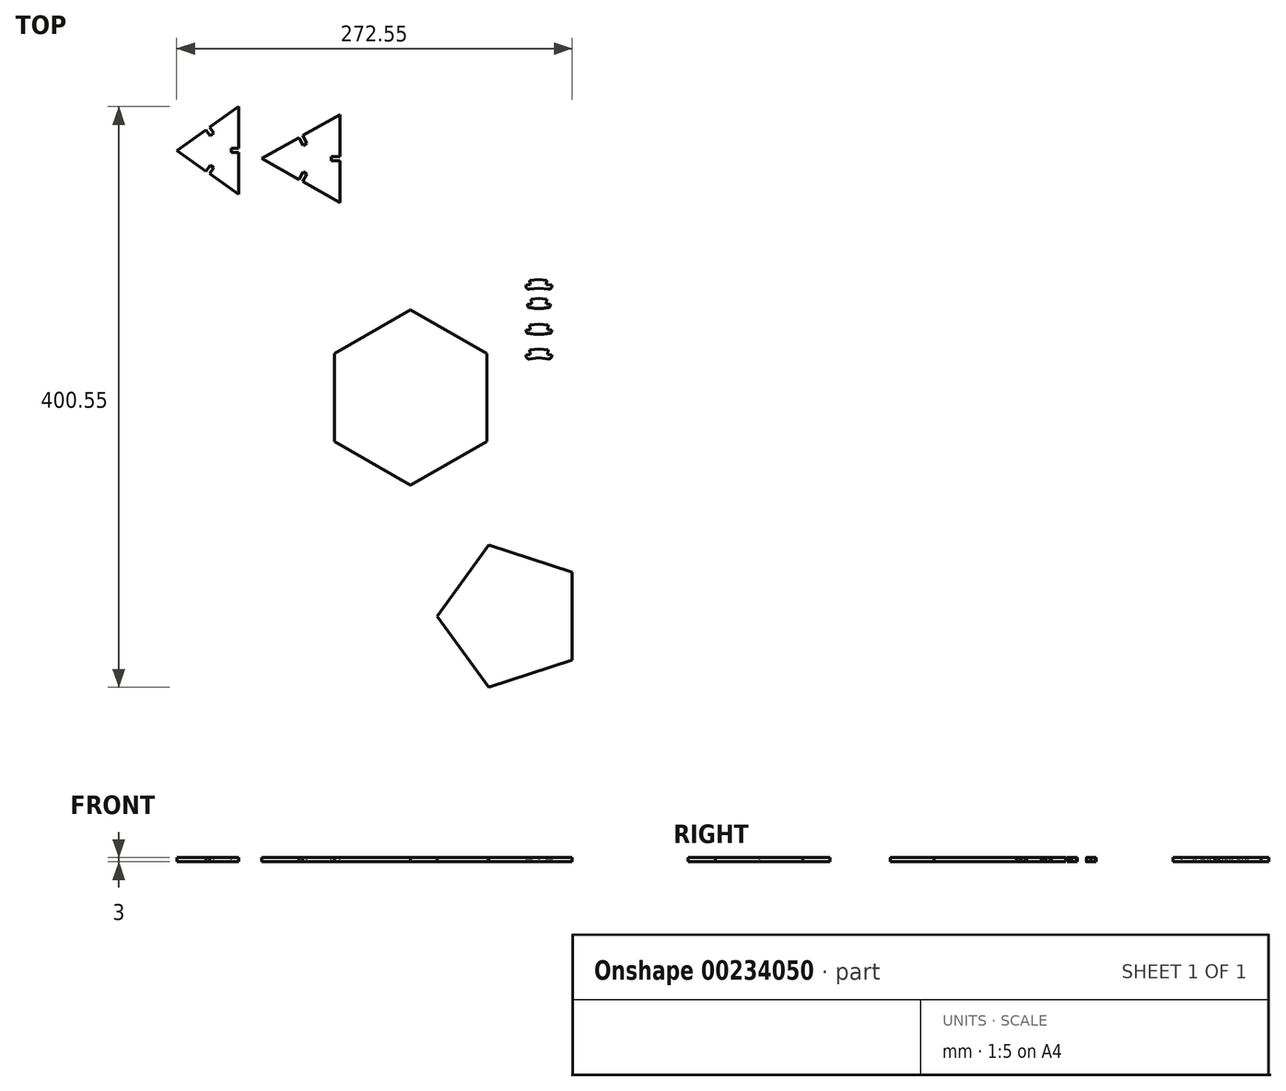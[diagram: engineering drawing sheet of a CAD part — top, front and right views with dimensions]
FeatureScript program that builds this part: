
annotation { "Feature Type Name" : "Feature", "Feature Type Description" : "" }
export const myFeature = defineFeature(function(context is Context, id is Id, definition is map)
    precondition{}
    {
        {
            var Q0;
            Q0=qCreatedBy(makeId("Top.planeOp"),FACE);
            var sketch = newSketch(context, id + "F0", { "sketchPlane" : qUnion([Q0])});
            skLineSegment(sketch, "E0", {"start": v(0, 0) * mm, "end": v(49.36, 17.26) * mm});
            skLineSegment(sketch, "E1", {"start": v(0, 0) * mm, "end": v(32.59, -40.9) * mm});
            skLineSegment(sketch, "E2", {"start": v(0, 0) * mm, "end": v(0, 52.3) * mm});
            skLineSegment(sketch, "E3", {"start": v(0, 52.3) * mm, "end": v(49.36, 17.26) * mm});
            skLineSegment(sketch, "E4", {"start": v(49.36, 17.26) * mm, "end": v(32.59, -40.9) * mm});
            skLineSegment(sketch, "E5", {"start": v(0, 0) * mm, "end": v(-27.84, -44.26) * mm});
            skLineSegment(sketch, "E6", {"start": v(-27.84, -44.26) * mm, "end": v(32.59, -40.9) * mm});
            skLineSegment(sketch, "E7", {"start": v(32.59, -40.9) * mm, "end": v(-27.84, -44.26) * mm});
            skLineSegment(sketch, "E8", {"start": v(-27.84, -44.26) * mm, "end": v(-50.97, 11.67) * mm});
            skLineSegment(sketch, "E9", {"start": v(-50.97, 11.67) * mm, "end": v(0, 0) * mm});
            skLineSegment(sketch, "E10", {"start": v(-50.97, 11.67) * mm, "end": v(-5.8, 51.97) * mm});
            skLineSegment(sketch, "E11", {"start": v(-5.8, 51.97) * mm, "end": v(0, 0) * mm});
            skLineSegment(sketch, "E12", {"start": v(-5.8, 51.97) * mm, "end": v(0, 52.3) * mm});
            skSolve(sketch);
        }
        {
            var Q0;
            Q0=qCreatedBy(makeId("Top.planeOp"),FACE);
            var sketch = newSketch(context, id + "F1", { "sketchPlane" : qUnion([Q0])});
            skLineSegment(sketch, "E13.0", {"start": v(0, 52.3) * mm, "end": v(49.36, 17.26) * mm});
            skLineSegment(sketch, "E14", {"start": v(0, 52.3) * mm, "end": v(55.9, 78.77) * mm});
            skLineSegment(sketch, "E15", {"start": v(55.9, 78.77) * mm, "end": v(49.36, 17.26) * mm});
            skLineSegment(sketch, "E16", {"start": v(55.9, 78.77) * mm, "end": v(104.98, 41.12) * mm});
            skLineSegment(sketch, "E17", {"start": v(104.98, 41.12) * mm, "end": v(49.36, 17.26) * mm});
            skLineSegment(sketch, "E18", {"start": v(55.9, 78.77) * mm, "end": v(4.16, 112.67) * mm});
            skLineSegment(sketch, "E19", {"start": v(4.16, 112.67) * mm, "end": v(0, 52.3) * mm});
            skLineSegment(sketch, "E20", {"start": v(55.9, 78.77) * mm, "end": v(57.85, 140.6) * mm});
            skLineSegment(sketch, "E21", {"start": v(57.85, 140.6) * mm, "end": v(4.16, 112.67) * mm});
            skLineSegment(sketch, "E22", {"start": v(55.9, 78.77) * mm, "end": v(113.62, 101.02) * mm});
            skLineSegment(sketch, "E23", {"start": v(113.62, 101.02) * mm, "end": v(104.98, 41.12) * mm});
            skLineSegment(sketch, "E24", {"start": v(55.9, 78.77) * mm, "end": v(67, 139.63) * mm});
            skLineSegment(sketch, "E25", {"start": v(67, 139.63) * mm, "end": v(113.62, 101.02) * mm});
            skLineSegment(sketch, "E26.0.2", {"start": v(49.36, 17.26) * mm, "end": v(0, 52.3) * mm, "construction": true});
            skLineSegment(sketch, "E27", {"start": v(67, 139.63) * mm, "end": v(124.73, 161.88) * mm});
            skLineSegment(sketch, "E28", {"start": v(124.73, 161.88) * mm, "end": v(113.62, 101.02) * mm});
            skLineSegment(sketch, "E29", {"start": v(67, 139.63) * mm, "end": v(75.65, 199.53) * mm});
            skLineSegment(sketch, "E30", {"start": v(75.65, 199.53) * mm, "end": v(124.73, 161.88) * mm});
            skLineSegment(sketch, "E31", {"start": v(113.62, 101.02) * mm, "end": v(170.87, 120.68) * mm});
            skLineSegment(sketch, "E32", {"start": v(170.87, 120.68) * mm, "end": v(124.73, 161.88) * mm});
            skLineSegment(sketch, "E33", {"start": v(4.16, 112.67) * mm, "end": v(11.33, 164.47) * mm});
            skLineSegment(sketch, "E34", {"start": v(11.33, 164.47) * mm, "end": v(57.85, 140.6) * mm});
            skLineSegment(sketch, "E35", {"start": v(67, 139.63) * mm, "end": v(29.12, 175.67) * mm});
            skLineSegment(sketch, "E36", {"start": v(29.12, 175.67) * mm, "end": v(75.65, 199.53) * mm});
            skLineSegment(sketch, "E37", {"start": v(104.98, 41.12) * mm, "end": v(151.5, 64.98) * mm});
            skLineSegment(sketch, "E38", {"start": v(151.5, 64.98) * mm, "end": v(113.62, 101.02) * mm});
            skLineSegment(sketch, "E39", {"start": v(113.62, 101.02) * mm, "end": v(156.1, 70.52) * mm});
            skLineSegment(sketch, "E40", {"start": v(156.1, 70.52) * mm, "end": v(170.87, 120.68) * mm});
            skLineSegment(sketch, "E41", {"start": v(156.1, 70.52) * mm, "end": v(206.92, 82.8) * mm});
            skLineSegment(sketch, "E42", {"start": v(206.92, 82.8) * mm, "end": v(170.87, 120.68) * mm});
            skLineSegment(sketch, "E43", {"start": v(0, 52.3) * mm, "end": v(0, 0) * mm});
            skLineSegment(sketch, "E44", {"start": v(0, 0) * mm, "end": v(49.36, 17.26) * mm});
            skLineSegment(sketch, "E45", {"start": v(124.73, 161.88) * mm, "end": v(131.27, 223.4) * mm});
            skLineSegment(sketch, "E46", {"start": v(124.73, 161.88) * mm, "end": v(180.63, 188.36) * mm});
            skLineSegment(sketch, "E47", {"start": v(75.65, 199.53) * mm, "end": v(131.27, 223.4) * mm});
            skLineSegment(sketch, "E48", {"start": v(180.63, 188.36) * mm, "end": v(176.47, 127.98) * mm});
            skLineSegment(sketch, "E49", {"start": v(176.47, 127.98) * mm, "end": v(124.73, 161.88) * mm});
            skLineSegment(sketch, "E50", {"start": v(131.27, 223.4) * mm, "end": v(180.63, 188.36) * mm});
            skLineSegment(sketch, "E51", {"start": v(75.65, 199.53) * mm, "end": v(82.2, 261.05) * mm});
            skLineSegment(sketch, "E52", {"start": v(82.2, 261.05) * mm, "end": v(131.27, 223.4) * mm});
            skLineSegment(sketch, "E53", {"start": v(176.47, 127.98) * mm, "end": v(232.38, 154.47) * mm});
            skLineSegment(sketch, "E54", {"start": v(232.38, 154.47) * mm, "end": v(180.63, 188.36) * mm});
            skLineSegment(sketch, "E55", {"start": v(176.47, 127.98) * mm, "end": v(225.83, 92.95) * mm});
            skLineSegment(sketch, "E56", {"start": v(225.83, 92.95) * mm, "end": v(232.38, 154.47) * mm});
            skLineSegment(sketch, "E57.1.0", {"start": v(0, 0) * mm, "end": v(21.73, -27.26) * mm});
            skLineSegment(sketch, "E57.1.1", {"start": v(48.98, -57.01) * mm, "end": v(21.73, -27.26) * mm});
            skLineSegment(sketch, "E57.1.2", {"start": v(61.88, -17.84) * mm, "end": v(21.73, -27.26) * mm});
            skLineSegment(sketch, "E57.1.3", {"start": v(21.73, -27.26) * mm, "end": v(32.9, 11.5) * mm, "construction": true});
            skLineSegment(sketch, "E57.1.4", {"start": v(48.98, -57.01) * mm, "end": v(74.24, -81.04) * mm});
            skLineSegment(sketch, "E57.1.5", {"start": v(88.58, -49.27) * mm, "end": v(48.98, -57.01) * mm});
            skLineSegment(sketch, "E57.1.6", {"start": v(32.9, 11.5) * mm, "end": v(61.88, -17.84) * mm});
            skLineSegment(sketch, "E57.1.7", {"start": v(71.82, 22.18) * mm, "end": v(32.9, 11.5) * mm});
            skLineSegment(sketch, "E57.1.8", {"start": v(61.88, -17.84) * mm, "end": v(48.98, -57.01) * mm});
            skLineSegment(sketch, "E57.1.9", {"start": v(78.73, -82.7) * mm, "end": v(113.55, -80.97) * mm});
            skLineSegment(sketch, "E57.1.10", {"start": v(61.88, -17.84) * mm, "end": v(102.62, -11.44) * mm});
            skLineSegment(sketch, "E57.1.11", {"start": v(119.38, -82.89) * mm, "end": v(108.2, -121.66) * mm});
            skLineSegment(sketch, "E57.1.12", {"start": v(61.88, -17.84) * mm, "end": v(71.82, 22.18) * mm});
            skLineSegment(sketch, "E57.1.13", {"start": v(61.88, -17.84) * mm, "end": v(88.58, -49.27) * mm});
            skLineSegment(sketch, "E57.1.14", {"start": v(88.58, -49.27) * mm, "end": v(113.55, -80.97) * mm});
            skLineSegment(sketch, "E57.1.15", {"start": v(108.2, -121.66) * mm, "end": v(148.35, -112.24) * mm});
            skLineSegment(sketch, "E57.1.16", {"start": v(102.62, -11.44) * mm, "end": v(88.58, -49.27) * mm});
            skLineSegment(sketch, "E57.1.17", {"start": v(129.32, -42.86) * mm, "end": v(88.58, -49.27) * mm});
            skLineSegment(sketch, "E57.1.18", {"start": v(97.65, -111.99) * mm, "end": v(113.55, -80.97) * mm});
            skLineSegment(sketch, "E57.1.19", {"start": v(61.88, -17.84) * mm, "end": v(101.21, -5.46) * mm});
            skLineSegment(sketch, "E57.1.20", {"start": v(71.82, 22.18) * mm, "end": v(106, 29.07) * mm});
            skLineSegment(sketch, "E57.1.21", {"start": v(101.21, -5.46) * mm, "end": v(71.82, 22.18) * mm});
            skLineSegment(sketch, "E57.1.22", {"start": v(119.38, -82.89) * mm, "end": v(148.35, -112.24) * mm});
            skLineSegment(sketch, "E57.1.23", {"start": v(158.3, -72.21) * mm, "end": v(119.38, -82.89) * mm});
            skLineSegment(sketch, "E57.1.24", {"start": v(102.62, -11.44) * mm, "end": v(129.32, -42.86) * mm});
            skLineSegment(sketch, "E57.1.25", {"start": v(106, 29.07) * mm, "end": v(101.21, -5.46) * mm});
            skLineSegment(sketch, "E57.1.26", {"start": v(102.62, -11.44) * mm, "end": v(142.21, -3.69) * mm});
            skLineSegment(sketch, "E57.1.27", {"start": v(148.35, -112.24) * mm, "end": v(158.3, -72.21) * mm});
            skLineSegment(sketch, "E57.1.28", {"start": v(142.21, -3.69) * mm, "end": v(129.32, -42.86) * mm});
            skLineSegment(sketch, "E57.1.29", {"start": v(129.32, -42.86) * mm, "end": v(158.3, -72.21) * mm});
            skLineSegment(sketch, "E57.1.30", {"start": v(129.32, -42.86) * mm, "end": v(169.47, -33.44) * mm});
            skLineSegment(sketch, "E57.1.31", {"start": v(116.96, 20.34) * mm, "end": v(142.21, -3.69) * mm});
            skLineSegment(sketch, "E57.1.32", {"start": v(142.21, -3.69) * mm, "end": v(169.47, -33.44) * mm});
            skLineSegment(sketch, "E57.1.33", {"start": v(142.21, -3.69) * mm, "end": v(182.36, 5.73) * mm});
            skLineSegment(sketch, "E57.1.34", {"start": v(169.47, -33.44) * mm, "end": v(158.3, -72.21) * mm});
            skLineSegment(sketch, "E57.1.35", {"start": v(182.36, 5.73) * mm, "end": v(169.47, -33.44) * mm});
            skLineSegment(sketch, "E57.1.36", {"start": v(32.9, 11.5) * mm, "end": v(21.73, -27.26) * mm});
            skLineSegment(sketch, "E57.1.37", {"start": v(74.24, -81.04) * mm, "end": v(88.58, -49.27) * mm});
            skLineSegment(sketch, "E57.1.38", {"start": v(78.73, -82.7) * mm, "end": v(97.65, -111.99) * mm});
            skLineSegment(sketch, "E57.1.39", {"start": v(88.58, -49.27) * mm, "end": v(78.73, -82.7) * mm});
            skLineSegment(sketch, "E57.1.40", {"start": v(113.55, -80.97) * mm, "end": v(129.32, -42.86) * mm});
            skLineSegment(sketch, "E57.1.41", {"start": v(119.38, -82.89) * mm, "end": v(129.32, -42.86) * mm});
            skLineSegment(sketch, "E57.1.42", {"start": v(102.62, -11.44) * mm, "end": v(116.96, 20.34) * mm});
            skLineSegment(sketch, "E57.2.0", {"start": v(0, 0) * mm, "end": v(-18.56, -29.5) * mm});
            skLineSegment(sketch, "E57.2.1", {"start": v(-37.65, -65.06) * mm, "end": v(-18.56, -29.5) * mm});
            skLineSegment(sketch, "E57.2.2", {"start": v(3.59, -64.3) * mm, "end": v(-18.56, -29.5) * mm});
            skLineSegment(sketch, "E57.2.3", {"start": v(-18.56, -29.5) * mm, "end": v(21.73, -27.26) * mm, "construction": true});
            skLineSegment(sketch, "E57.2.4", {"start": v(-37.65, -65.06) * mm, "end": v(-51.99, -96.83) * mm});
            skLineSegment(sketch, "E57.2.5", {"start": v(-17.26, -99.88) * mm, "end": v(-37.65, -65.06) * mm});
            skLineSegment(sketch, "E57.2.6", {"start": v(21.73, -27.26) * mm, "end": v(3.59, -64.3) * mm});
            skLineSegment(sketch, "E57.2.7", {"start": v(44.65, -60.47) * mm, "end": v(21.73, -27.26) * mm});
            skLineSegment(sketch, "E57.2.8", {"start": v(3.59, -64.3) * mm, "end": v(-37.65, -65.06) * mm});
            skLineSegment(sketch, "E57.2.9", {"start": v(-52.08, -101.62) * mm, "end": v(-38.94, -133.91) * mm});
            skLineSegment(sketch, "E57.2.10", {"start": v(3.59, -64.3) * mm, "end": v(23.08, -100.64) * mm});
            skLineSegment(sketch, "E57.2.11", {"start": v(-38.83, -140.05) * mm, "end": v(-79.11, -142.3) * mm});
            skLineSegment(sketch, "E57.2.12", {"start": v(3.59, -64.3) * mm, "end": v(44.65, -60.47) * mm});
            skLineSegment(sketch, "E57.2.13", {"start": v(3.59, -64.3) * mm, "end": v(-17.26, -99.88) * mm});
            skLineSegment(sketch, "E57.2.14", {"start": v(-17.26, -99.88) * mm, "end": v(-38.94, -133.91) * mm});
            skLineSegment(sketch, "E57.2.15", {"start": v(-79.11, -142.3) * mm, "end": v(-56.97, -177.08) * mm});
            skLineSegment(sketch, "E57.2.16", {"start": v(23.08, -100.64) * mm, "end": v(-17.26, -99.88) * mm});
            skLineSegment(sketch, "E57.2.17", {"start": v(2.23, -136.22) * mm, "end": v(-17.26, -99.88) * mm});
            skLineSegment(sketch, "E57.2.18", {"start": v(-73.47, -129.14) * mm, "end": v(-38.94, -133.91) * mm});
            skLineSegment(sketch, "E57.2.19", {"start": v(3.59, -64.3) * mm, "end": v(28.26, -97.34) * mm});
            skLineSegment(sketch, "E57.2.20", {"start": v(44.65, -60.47) * mm, "end": v(62.43, -90.45) * mm});
            skLineSegment(sketch, "E57.2.21", {"start": v(28.26, -97.34) * mm, "end": v(44.65, -60.47) * mm});
            skLineSegment(sketch, "E57.2.22", {"start": v(-38.83, -140.05) * mm, "end": v(-56.97, -177.08) * mm});
            skLineSegment(sketch, "E57.2.23", {"start": v(-15.9, -173.26) * mm, "end": v(-38.83, -140.05) * mm});
            skLineSegment(sketch, "E57.2.24", {"start": v(23.08, -100.64) * mm, "end": v(2.23, -136.22) * mm});
            skLineSegment(sketch, "E57.2.25", {"start": v(62.43, -90.45) * mm, "end": v(28.26, -97.34) * mm});
            skLineSegment(sketch, "E57.2.26", {"start": v(23.08, -100.64) * mm, "end": v(43.47, -135.46) * mm});
            skLineSegment(sketch, "E57.2.27", {"start": v(-56.97, -177.08) * mm, "end": v(-15.9, -173.26) * mm});
            skLineSegment(sketch, "E57.2.28", {"start": v(43.47, -135.46) * mm, "end": v(2.23, -136.22) * mm});
            skLineSegment(sketch, "E57.2.29", {"start": v(2.23, -136.22) * mm, "end": v(-15.9, -173.26) * mm});
            skLineSegment(sketch, "E57.2.30", {"start": v(2.23, -136.22) * mm, "end": v(24.38, -171) * mm});
            skLineSegment(sketch, "E57.2.31", {"start": v(57.8, -103.69) * mm, "end": v(43.47, -135.46) * mm});
            skLineSegment(sketch, "E57.2.32", {"start": v(43.47, -135.46) * mm, "end": v(24.38, -171) * mm});
            skLineSegment(sketch, "E57.2.33", {"start": v(43.47, -135.46) * mm, "end": v(65.61, -170.25) * mm});
            skLineSegment(sketch, "E57.2.34", {"start": v(24.38, -171) * mm, "end": v(-15.9, -173.26) * mm});
            skLineSegment(sketch, "E57.2.35", {"start": v(65.61, -170.25) * mm, "end": v(24.38, -171) * mm});
            skLineSegment(sketch, "E57.2.36", {"start": v(21.73, -27.26) * mm, "end": v(-18.56, -29.5) * mm});
            skLineSegment(sketch, "E57.2.37", {"start": v(-51.99, -96.83) * mm, "end": v(-17.26, -99.88) * mm});
            skLineSegment(sketch, "E57.2.38", {"start": v(-52.08, -101.62) * mm, "end": v(-73.47, -129.14) * mm});
            skLineSegment(sketch, "E57.2.39", {"start": v(-17.26, -99.88) * mm, "end": v(-52.08, -101.62) * mm});
            skLineSegment(sketch, "E57.2.40", {"start": v(-38.94, -133.91) * mm, "end": v(2.23, -136.22) * mm});
            skLineSegment(sketch, "E57.2.41", {"start": v(-38.83, -140.05) * mm, "end": v(2.23, -136.22) * mm});
            skLineSegment(sketch, "E57.2.42", {"start": v(23.08, -100.64) * mm, "end": v(57.8, -103.69) * mm});
            skLineSegment(sketch, "E57.3.0", {"start": v(0, 0) * mm, "end": v(-33.98, 7.78) * mm});
            skLineSegment(sketch, "E57.3.1", {"start": v(-73.84, 14.06) * mm, "end": v(-33.98, 7.78) * mm});
            skLineSegment(sketch, "E57.3.2", {"start": v(-59.5, -24.61) * mm, "end": v(-33.98, 7.78) * mm});
            skLineSegment(sketch, "E57.3.3", {"start": v(-33.98, 7.78) * mm, "end": v(-18.56, -29.5) * mm, "construction": true});
            skLineSegment(sketch, "E57.3.4", {"start": v(-73.84, 14.06) * mm, "end": v(-108.57, 17.1) * mm});
            skLineSegment(sketch, "E57.3.5", {"start": v(-99.98, -16.68) * mm, "end": v(-73.84, 14.06) * mm});
            skLineSegment(sketch, "E57.3.6", {"start": v(-18.56, -29.5) * mm, "end": v(-59.5, -24.61) * mm});
            skLineSegment(sketch, "E57.3.7", {"start": v(-42.34, -62.1) * mm, "end": v(-18.56, -29.5) * mm});
            skLineSegment(sketch, "E57.3.8", {"start": v(-59.5, -24.61) * mm, "end": v(-73.84, 14.06) * mm});
            skLineSegment(sketch, "E57.3.9", {"start": v(-113.12, 15.6) * mm, "end": v(-139.26, -7.45) * mm});
            skLineSegment(sketch, "E57.3.10", {"start": v(-59.5, -24.61) * mm, "end": v(-87.38, -55.01) * mm});
            skLineSegment(sketch, "E57.3.11", {"start": v(-145.01, -9.58) * mm, "end": v(-160.44, 27.7) * mm});
            skLineSegment(sketch, "E57.3.12", {"start": v(-59.5, -24.61) * mm, "end": v(-42.34, -62.1) * mm});
            skLineSegment(sketch, "E57.3.13", {"start": v(-59.5, -24.61) * mm, "end": v(-99.98, -16.68) * mm});
            skLineSegment(sketch, "E57.3.14", {"start": v(-99.98, -16.68) * mm, "end": v(-139.26, -7.45) * mm});
            skLineSegment(sketch, "E57.3.15", {"start": v(-160.44, 27.7) * mm, "end": v(-185.96, -4.69) * mm});
            skLineSegment(sketch, "E57.3.16", {"start": v(-87.38, -55.01) * mm, "end": v(-99.98, -16.68) * mm});
            skLineSegment(sketch, "E57.3.17", {"start": v(-127.85, -47.08) * mm, "end": v(-99.98, -16.68) * mm});
            skLineSegment(sketch, "E57.3.18", {"start": v(-146.16, 26.72) * mm, "end": v(-139.26, -7.45) * mm});
            skLineSegment(sketch, "E57.3.19", {"start": v(-59.5, -24.61) * mm, "end": v(-82.55, -58.81) * mm});
            skLineSegment(sketch, "E57.3.20", {"start": v(-42.34, -62.1) * mm, "end": v(-64.77, -88.8) * mm});
            skLineSegment(sketch, "E57.3.21", {"start": v(-82.55, -58.81) * mm, "end": v(-42.34, -62.1) * mm});
            skLineSegment(sketch, "E57.3.22", {"start": v(-145.01, -9.58) * mm, "end": v(-185.96, -4.69) * mm});
            skLineSegment(sketch, "E57.3.23", {"start": v(-168.8, -42.18) * mm, "end": v(-145.01, -9.58) * mm});
            skLineSegment(sketch, "E57.3.24", {"start": v(-87.38, -55.01) * mm, "end": v(-127.85, -47.08) * mm});
            skLineSegment(sketch, "E57.3.25", {"start": v(-64.77, -88.8) * mm, "end": v(-82.55, -58.81) * mm});
            skLineSegment(sketch, "E57.3.26", {"start": v(-87.38, -55.01) * mm, "end": v(-113.51, -85.75) * mm});
            skLineSegment(sketch, "E57.3.27", {"start": v(-185.96, -4.69) * mm, "end": v(-168.8, -42.18) * mm});
            skLineSegment(sketch, "E57.3.28", {"start": v(-113.51, -85.75) * mm, "end": v(-127.85, -47.08) * mm});
            skLineSegment(sketch, "E57.3.29", {"start": v(-127.85, -47.08) * mm, "end": v(-168.8, -42.18) * mm});
            skLineSegment(sketch, "E57.3.30", {"start": v(-127.85, -47.08) * mm, "end": v(-153.37, -79.47) * mm});
            skLineSegment(sketch, "E57.3.31", {"start": v(-78.79, -88.8) * mm, "end": v(-113.51, -85.75) * mm});
            skLineSegment(sketch, "E57.3.32", {"start": v(-113.51, -85.75) * mm, "end": v(-153.37, -79.47) * mm});
            skLineSegment(sketch, "E57.3.33", {"start": v(-113.51, -85.75) * mm, "end": v(-139.04, -118.14) * mm});
            skLineSegment(sketch, "E57.3.34", {"start": v(-153.37, -79.47) * mm, "end": v(-168.8, -42.18) * mm});
            skLineSegment(sketch, "E57.3.35", {"start": v(-139.04, -118.14) * mm, "end": v(-153.37, -79.47) * mm});
            skLineSegment(sketch, "E57.3.36", {"start": v(-18.56, -29.5) * mm, "end": v(-33.98, 7.78) * mm});
            skLineSegment(sketch, "E57.3.37", {"start": v(-108.57, 17.1) * mm, "end": v(-99.98, -16.68) * mm});
            skLineSegment(sketch, "E57.3.38", {"start": v(-113.12, 15.6) * mm, "end": v(-146.16, 26.72) * mm});
            skLineSegment(sketch, "E57.3.39", {"start": v(-99.98, -16.68) * mm, "end": v(-113.12, 15.6) * mm});
            skLineSegment(sketch, "E57.3.40", {"start": v(-139.26, -7.45) * mm, "end": v(-127.85, -47.08) * mm});
            skLineSegment(sketch, "E57.3.41", {"start": v(-145.01, -9.58) * mm, "end": v(-127.85, -47.08) * mm});
            skLineSegment(sketch, "E57.3.42", {"start": v(-87.38, -55.01) * mm, "end": v(-78.79, -88.8) * mm});
            skLineSegment(sketch, "E57.4.0", {"start": v(0, 0) * mm, "end": v(-3.88, 34.64) * mm});
            skLineSegment(sketch, "E57.4.1", {"start": v(-11.1, 74.34) * mm, "end": v(-3.88, 34.64) * mm});
            skLineSegment(sketch, "E57.4.2", {"start": v(-42.88, 48.05) * mm, "end": v(-3.88, 34.64) * mm});
            skLineSegment(sketch, "E57.4.3", {"start": v(-3.88, 52.07) * mm, "end": v(-33.98, 25.2) * mm, "construction": true});
            skLineSegment(sketch, "E57.4.4", {"start": v(-11.1, 74.34) * mm, "end": v(-19.7, 108.13) * mm});
            skLineSegment(sketch, "E57.4.5", {"start": v(-48.75, 88.87) * mm, "end": v(-11.1, 74.34) * mm});
            skLineSegment(sketch, "E57.4.6", {"start": v(-33.98, 7.78) * mm, "end": v(-42.88, 48.05) * mm});
            skLineSegment(sketch, "E57.4.7", {"start": v(-72.6, 19.46) * mm, "end": v(-33.98, 7.78) * mm});
            skLineSegment(sketch, "E57.4.8", {"start": v(-42.88, 48.05) * mm, "end": v(-11.1, 74.34) * mm});
            skLineSegment(sketch, "E57.4.9", {"start": v(-22.61, 111.93) * mm, "end": v(-53, 129) * mm});
            skLineSegment(sketch, "E57.4.10", {"start": v(-42.88, 48.05) * mm, "end": v(-80.77, 64.31) * mm});
            skLineSegment(sketch, "E57.4.11", {"start": v(-56.92, 133.72) * mm, "end": v(-26.82, 160.59) * mm});
            skLineSegment(sketch, "E57.4.12", {"start": v(-42.88, 48.05) * mm, "end": v(-72.6, 19.46) * mm});
            skLineSegment(sketch, "E57.4.13", {"start": v(-42.88, 48.05) * mm, "end": v(-48.75, 88.87) * mm});
            skLineSegment(sketch, "E57.4.14", {"start": v(-48.75, 88.87) * mm, "end": v(-53, 129) * mm});
            skLineSegment(sketch, "E57.4.15", {"start": v(-26.82, 160.59) * mm, "end": v(-65.82, 173.99) * mm});
            skLineSegment(sketch, "E57.4.16", {"start": v(-80.77, 64.31) * mm, "end": v(-48.75, 88.87) * mm});
            skLineSegment(sketch, "E57.4.17", {"start": v(-86.65, 105.13) * mm, "end": v(-48.75, 88.87) * mm});
            skLineSegment(sketch, "E57.4.18", {"start": v(-23.03, 146.78) * mm, "end": v(-53, 129) * mm});
            skLineSegment(sketch, "E57.4.19", {"start": v(-42.88, 48.05) * mm, "end": v(-82.77, 58.5) * mm});
            skLineSegment(sketch, "E57.4.20", {"start": v(-72.6, 19.46) * mm, "end": v(-105.2, 31.82) * mm});
            skLineSegment(sketch, "E57.4.21", {"start": v(-82.77, 58.5) * mm, "end": v(-72.6, 19.46) * mm});
            skLineSegment(sketch, "E57.4.22", {"start": v(-56.92, 133.72) * mm, "end": v(-65.82, 173.99) * mm});
            skLineSegment(sketch, "E57.4.23", {"start": v(-95.54, 145.4) * mm, "end": v(-56.92, 133.72) * mm});
            skLineSegment(sketch, "E57.4.24", {"start": v(-80.77, 64.31) * mm, "end": v(-86.65, 105.13) * mm});
            skLineSegment(sketch, "E57.4.25", {"start": v(-105.2, 31.82) * mm, "end": v(-82.77, 58.5) * mm});
            skLineSegment(sketch, "E57.4.26", {"start": v(-80.77, 64.31) * mm, "end": v(-118.42, 78.84) * mm});
            skLineSegment(sketch, "E57.4.27", {"start": v(-65.82, 173.99) * mm, "end": v(-95.54, 145.4) * mm});
            skLineSegment(sketch, "E57.4.28", {"start": v(-118.42, 78.84) * mm, "end": v(-86.65, 105.13) * mm});
            skLineSegment(sketch, "E57.4.29", {"start": v(-86.65, 105.13) * mm, "end": v(-95.54, 145.4) * mm});
            skLineSegment(sketch, "E57.4.30", {"start": v(-86.65, 105.13) * mm, "end": v(-125.65, 118.54) * mm});
            skLineSegment(sketch, "E57.4.31", {"start": v(-109.83, 45.05) * mm, "end": v(-118.42, 78.84) * mm});
            skLineSegment(sketch, "E57.4.32", {"start": v(-118.42, 78.84) * mm, "end": v(-125.65, 118.54) * mm});
            skLineSegment(sketch, "E57.4.33", {"start": v(-118.42, 78.84) * mm, "end": v(-157.42, 92.24) * mm});
            skLineSegment(sketch, "E57.4.34", {"start": v(-125.65, 118.54) * mm, "end": v(-95.54, 145.4) * mm});
            skLineSegment(sketch, "E57.4.35", {"start": v(-157.42, 92.24) * mm, "end": v(-125.65, 118.54) * mm});
            skLineSegment(sketch, "E57.4.36", {"start": v(-33.98, 7.78) * mm, "end": v(-3.88, 34.64) * mm});
            skLineSegment(sketch, "E57.4.37", {"start": v(-19.7, 108.13) * mm, "end": v(-48.75, 88.87) * mm});
            skLineSegment(sketch, "E57.4.38", {"start": v(-22.61, 111.93) * mm, "end": v(-23.03, 146.78) * mm});
            skLineSegment(sketch, "E57.4.39", {"start": v(-48.75, 88.87) * mm, "end": v(-22.61, 111.93) * mm});
            skLineSegment(sketch, "E57.4.40", {"start": v(-53, 129) * mm, "end": v(-86.65, 105.13) * mm});
            skLineSegment(sketch, "E57.4.41", {"start": v(-56.92, 133.72) * mm, "end": v(-86.65, 105.13) * mm});
            skLineSegment(sketch, "E57.4.42", {"start": v(-80.77, 64.31) * mm, "end": v(-109.83, 45.05) * mm});
            skPoint(sketch, "E57.center", {"position": v(0, 17.43) * mm});
            skLineSegment(sketch, "E57.anchor1", {"start": v(0, 17.43) * mm, "end": v(0, 52.3) * mm, "construction": true});
            skLineSegment(sketch, "E57.anchor2", {"start": v(0, 17.43) * mm, "end": v(-33.98, 25.2) * mm, "construction": true});
            skSolve(sketch);
        }
        {
            var Q0;
            Q0=qCreatedBy(makeId("Top.planeOp"),FACE);
            var sketch = newSketch(context, id + "F2", { "sketchPlane" : qUnion([Q0])});
            skLineSegment(sketch, "E58.0", {"start": v(-65.82, 173.99) * mm, "end": v(-95.54, 145.4) * mm});
            skLineSegment(sketch, "E59.0", {"start": v(-26.82, 160.59) * mm, "end": v(-65.82, 173.99) * mm});
            skLineSegment(sketch, "E60.0", {"start": v(-56.92, 133.72) * mm, "end": v(-26.82, 160.59) * mm});
            skLineSegment(sketch, "E61.0", {"start": v(-56.92, 133.72) * mm, "end": v(-86.65, 105.13) * mm});
            skLineSegment(sketch, "E62.0", {"start": v(-53, 129) * mm, "end": v(-86.65, 105.13) * mm});
            skLineSegment(sketch, "E63.0", {"start": v(-23.03, 146.78) * mm, "end": v(-53, 129) * mm});
            skLineSegment(sketch, "E64.0", {"start": v(-22.61, 111.93) * mm, "end": v(-23.03, 146.78) * mm});
            skLineSegment(sketch, "E65.0", {"start": v(-48.75, 88.87) * mm, "end": v(-22.61, 111.93) * mm});
            skLineSegment(sketch, "E66.0", {"start": v(-19.7, 108.13) * mm, "end": v(-48.75, 88.87) * mm});
            skLineSegment(sketch, "E67.0", {"start": v(-11.1, 74.34) * mm, "end": v(-19.7, 108.13) * mm});
            skLineSegment(sketch, "E68.0", {"start": v(-11.1, 74.34) * mm, "end": v(-3.88, 34.64) * mm});
            skLineSegment(sketch, "E69.0", {"start": v(0, 0) * mm, "end": v(-3.88, 34.64) * mm});
            skLineSegment(sketch, "E70.0", {"start": v(0, 52.3) * mm, "end": v(0, 0) * mm});
            skLineSegment(sketch, "E71.0", {"start": v(4.16, 112.67) * mm, "end": v(0, 52.3) * mm});
            skLineSegment(sketch, "E72.0", {"start": v(4.16, 112.67) * mm, "end": v(11.33, 164.47) * mm});
            skLineSegment(sketch, "E73.0", {"start": v(11.33, 164.47) * mm, "end": v(57.85, 140.6) * mm});
            skLineSegment(sketch, "E74.0", {"start": v(55.9, 78.77) * mm, "end": v(57.85, 140.6) * mm});
            skLineSegment(sketch, "E75.0", {"start": v(55.9, 78.77) * mm, "end": v(67, 139.63) * mm});
            skLineSegment(sketch, "E76.0", {"start": v(67, 139.63) * mm, "end": v(29.12, 175.67) * mm});
            skLineSegment(sketch, "E77.0", {"start": v(29.12, 175.67) * mm, "end": v(75.65, 199.53) * mm});
            skLineSegment(sketch, "E78.0", {"start": v(75.65, 199.53) * mm, "end": v(82.2, 261.05) * mm});
            skLineSegment(sketch, "E79.0", {"start": v(82.2, 261.05) * mm, "end": v(131.27, 223.4) * mm});
            skLineSegment(sketch, "E80.0", {"start": v(131.27, 223.4) * mm, "end": v(180.63, 188.36) * mm});
            skLineSegment(sketch, "E81.0", {"start": v(232.38, 154.47) * mm, "end": v(180.63, 188.36) * mm});
            skLineSegment(sketch, "E82.0", {"start": v(225.83, 92.95) * mm, "end": v(232.38, 154.47) * mm});
            skLineSegment(sketch, "E83.0", {"start": v(176.47, 127.98) * mm, "end": v(225.83, 92.95) * mm});
            skLineSegment(sketch, "E84.0", {"start": v(176.47, 127.98) * mm, "end": v(124.73, 161.88) * mm});
            skLineSegment(sketch, "E85.0", {"start": v(170.87, 120.68) * mm, "end": v(124.73, 161.88) * mm});
            skLineSegment(sketch, "E86.0", {"start": v(206.92, 82.8) * mm, "end": v(170.87, 120.68) * mm});
            skLineSegment(sketch, "E87.0", {"start": v(156.1, 70.52) * mm, "end": v(206.92, 82.8) * mm});
            skLineSegment(sketch, "E88.0", {"start": v(113.62, 101.02) * mm, "end": v(156.1, 70.52) * mm});
            skLineSegment(sketch, "E89.0", {"start": v(151.5, 64.98) * mm, "end": v(113.62, 101.02) * mm});
            skLineSegment(sketch, "E90.0", {"start": v(104.98, 41.12) * mm, "end": v(151.5, 64.98) * mm});
            skLineSegment(sketch, "E91.0", {"start": v(104.98, 41.12) * mm, "end": v(49.36, 17.26) * mm});
            skLineSegment(sketch, "E92.0", {"start": v(71.82, 22.18) * mm, "end": v(32.9, 11.5) * mm});
            skLineSegment(sketch, "E93.0", {"start": v(71.82, 22.18) * mm, "end": v(106, 29.07) * mm});
            skLineSegment(sketch, "E94.0", {"start": v(106, 29.07) * mm, "end": v(101.21, -5.46) * mm});
            skLineSegment(sketch, "E95.0", {"start": v(61.88, -17.84) * mm, "end": v(101.21, -5.46) * mm});
            skLineSegment(sketch, "E96.0", {"start": v(61.88, -17.84) * mm, "end": v(102.62, -11.44) * mm});
            skLineSegment(sketch, "E97.0", {"start": v(102.62, -11.44) * mm, "end": v(116.96, 20.34) * mm});
            skLineSegment(sketch, "E98.0", {"start": v(116.96, 20.34) * mm, "end": v(142.21, -3.69) * mm});
            skLineSegment(sketch, "E99.0", {"start": v(142.21, -3.69) * mm, "end": v(182.36, 5.73) * mm});
            skLineSegment(sketch, "E100.0", {"start": v(182.36, 5.73) * mm, "end": v(169.47, -33.44) * mm});
            skLineSegment(sketch, "E101.0", {"start": v(169.47, -33.44) * mm, "end": v(158.3, -72.21) * mm});
            skLineSegment(sketch, "E102.0", {"start": v(148.35, -112.24) * mm, "end": v(158.3, -72.21) * mm});
            skLineSegment(sketch, "E103.0", {"start": v(108.2, -121.66) * mm, "end": v(148.35, -112.24) * mm});
            skLineSegment(sketch, "E104.0", {"start": v(119.38, -82.89) * mm, "end": v(108.2, -121.66) * mm});
            skLineSegment(sketch, "E105.0", {"start": v(119.38, -82.89) * mm, "end": v(129.32, -42.86) * mm});
            skLineSegment(sketch, "E106.0", {"start": v(113.55, -80.97) * mm, "end": v(129.32, -42.86) * mm});
            skLineSegment(sketch, "E107.0", {"start": v(97.65, -111.99) * mm, "end": v(113.55, -80.97) * mm});
            skLineSegment(sketch, "E108.0", {"start": v(78.73, -82.7) * mm, "end": v(97.65, -111.99) * mm});
            skLineSegment(sketch, "E109.0", {"start": v(88.58, -49.27) * mm, "end": v(78.73, -82.7) * mm});
            skLineSegment(sketch, "E110.0", {"start": v(48.98, -57.01) * mm, "end": v(74.24, -81.04) * mm});
            skLineSegment(sketch, "E111.0", {"start": v(48.98, -57.01) * mm, "end": v(21.73, -27.26) * mm});
            skLineSegment(sketch, "E112.0", {"start": v(44.65, -60.47) * mm, "end": v(21.73, -27.26) * mm});
            skLineSegment(sketch, "E113.0", {"start": v(44.65, -60.47) * mm, "end": v(62.43, -90.45) * mm});
            skLineSegment(sketch, "E114.0", {"start": v(62.43, -90.45) * mm, "end": v(28.26, -97.34) * mm});
            skLineSegment(sketch, "E115.0", {"start": v(3.59, -64.3) * mm, "end": v(28.26, -97.34) * mm});
            skLineSegment(sketch, "E116.0", {"start": v(3.59, -64.3) * mm, "end": v(23.08, -100.64) * mm});
            skLineSegment(sketch, "E117.0", {"start": v(23.08, -100.64) * mm, "end": v(57.8, -103.69) * mm});
            skLineSegment(sketch, "E118.0", {"start": v(57.8, -103.69) * mm, "end": v(43.47, -135.46) * mm});
            skLineSegment(sketch, "E119.0", {"start": v(43.47, -135.46) * mm, "end": v(65.61, -170.25) * mm});
            skLineSegment(sketch, "E120.0", {"start": v(65.61, -170.25) * mm, "end": v(24.38, -171) * mm});
            skLineSegment(sketch, "E121.0", {"start": v(24.38, -171) * mm, "end": v(-15.9, -173.26) * mm});
            skLineSegment(sketch, "E122.0", {"start": v(-56.97, -177.08) * mm, "end": v(-15.9, -173.26) * mm});
            skLineSegment(sketch, "E123.0", {"start": v(-79.11, -142.3) * mm, "end": v(-56.97, -177.08) * mm});
            skLineSegment(sketch, "E124.0", {"start": v(-38.83, -140.05) * mm, "end": v(-79.11, -142.3) * mm});
            skLineSegment(sketch, "E125.0", {"start": v(-38.83, -140.05) * mm, "end": v(2.23, -136.22) * mm});
            skLineSegment(sketch, "E126.0", {"start": v(-38.94, -133.91) * mm, "end": v(2.23, -136.22) * mm});
            skLineSegment(sketch, "E127.0", {"start": v(-73.47, -129.14) * mm, "end": v(-38.94, -133.91) * mm});
            skLineSegment(sketch, "E128.0", {"start": v(-52.08, -101.62) * mm, "end": v(-73.47, -129.14) * mm});
            skLineSegment(sketch, "E129.0", {"start": v(-17.26, -99.88) * mm, "end": v(-52.08, -101.62) * mm});
            skLineSegment(sketch, "E130.0", {"start": v(-51.99, -96.83) * mm, "end": v(-17.26, -99.88) * mm});
            skLineSegment(sketch, "E131.0", {"start": v(-37.65, -65.06) * mm, "end": v(-51.99, -96.83) * mm});
            skLineSegment(sketch, "E132.0", {"start": v(-37.65, -65.06) * mm, "end": v(-18.56, -29.5) * mm});
            skLineSegment(sketch, "E133.0", {"start": v(-42.34, -62.1) * mm, "end": v(-18.56, -29.5) * mm});
            skLineSegment(sketch, "E134.0", {"start": v(-42.34, -62.1) * mm, "end": v(-64.77, -88.8) * mm});
            skLineSegment(sketch, "E135.0", {"start": v(-64.77, -88.8) * mm, "end": v(-82.55, -58.81) * mm});
            skLineSegment(sketch, "E136.0", {"start": v(-59.5, -24.61) * mm, "end": v(-82.55, -58.81) * mm});
            skLineSegment(sketch, "E137.0", {"start": v(-59.5, -24.61) * mm, "end": v(-87.38, -55.01) * mm});
            skLineSegment(sketch, "E138.0", {"start": v(-87.38, -55.01) * mm, "end": v(-78.79, -88.8) * mm});
            skLineSegment(sketch, "E139.0", {"start": v(-78.79, -88.8) * mm, "end": v(-113.51, -85.75) * mm});
            skLineSegment(sketch, "E140.0", {"start": v(-113.51, -85.75) * mm, "end": v(-139.04, -118.14) * mm});
            skLineSegment(sketch, "E141.0", {"start": v(-139.04, -118.14) * mm, "end": v(-153.37, -79.47) * mm});
            skLineSegment(sketch, "E142.0", {"start": v(-153.37, -79.47) * mm, "end": v(-168.8, -42.18) * mm});
            skLineSegment(sketch, "E143.0", {"start": v(-185.96, -4.69) * mm, "end": v(-168.8, -42.18) * mm});
            skLineSegment(sketch, "E144.0", {"start": v(-160.44, 27.7) * mm, "end": v(-185.96, -4.69) * mm});
            skLineSegment(sketch, "E145.0", {"start": v(-145.01, -9.58) * mm, "end": v(-127.85, -47.08) * mm});
            skLineSegment(sketch, "E146.0", {"start": v(-139.26, -7.45) * mm, "end": v(-127.85, -47.08) * mm});
            skLineSegment(sketch, "E147.0", {"start": v(-146.16, 26.72) * mm, "end": v(-139.26, -7.45) * mm});
            skLineSegment(sketch, "E148.0", {"start": v(-113.12, 15.6) * mm, "end": v(-146.16, 26.72) * mm});
            skLineSegment(sketch, "E149.0", {"start": v(-99.98, -16.68) * mm, "end": v(-113.12, 15.6) * mm});
            skLineSegment(sketch, "E150.0", {"start": v(-108.57, 17.1) * mm, "end": v(-99.98, -16.68) * mm});
            skLineSegment(sketch, "E151.0", {"start": v(-73.84, 14.06) * mm, "end": v(-108.57, 17.1) * mm});
            skLineSegment(sketch, "E152.0", {"start": v(-73.84, 14.06) * mm, "end": v(-33.98, 7.78) * mm});
            skLineSegment(sketch, "E153.0", {"start": v(-72.6, 19.46) * mm, "end": v(-33.98, 7.78) * mm});
            skLineSegment(sketch, "E154.0", {"start": v(-72.6, 19.46) * mm, "end": v(-105.2, 31.82) * mm});
            skLineSegment(sketch, "E155.0", {"start": v(-105.2, 31.82) * mm, "end": v(-82.77, 58.5) * mm});
            skLineSegment(sketch, "E156.0", {"start": v(-42.88, 48.05) * mm, "end": v(-82.77, 58.5) * mm});
            skLineSegment(sketch, "E157.0", {"start": v(-42.88, 48.05) * mm, "end": v(-80.77, 64.31) * mm});
            skLineSegment(sketch, "E158.0", {"start": v(-80.77, 64.31) * mm, "end": v(-109.83, 45.05) * mm});
            skPoint(sketch, "E159.0", {"position": v(-114.12, 61.95) * mm});
            skLineSegment(sketch, "E160.0", {"start": v(-118.42, 78.84) * mm, "end": v(-157.42, 92.24) * mm});
            skLineSegment(sketch, "E161.0", {"start": v(-109.83, 45.05) * mm, "end": v(-118.42, 78.84) * mm});
            skLineSegment(sketch, "E162.0", {"start": v(-157.42, 92.24) * mm, "end": v(-125.65, 118.54) * mm});
            skLineSegment(sketch, "E163.0", {"start": v(-125.65, 118.54) * mm, "end": v(-95.54, 145.4) * mm});
            skLineSegment(sketch, "E164.0", {"start": v(-145.01, -9.58) * mm, "end": v(-160.44, 27.7) * mm});
            skPoint(sketch, "E165.0", {"position": v(81.41, -65.15) * mm});
            skLineSegment(sketch, "E166.0", {"start": v(74.24, -81.04) * mm, "end": v(88.58, -49.27) * mm});
            skSolve(sketch);
        }
        {
            var Q0;
            Q0=qCreatedBy(makeId("Top.planeOp"),FACE);
            var sketch = newSketch(context, id + "F3", { "sketchPlane" : qUnion([Q0])});
            skCircle(sketch, "E167.cCircle", {"center": v(417.98, -116.83) * mm, "radius": 52.42 * mm, "construction": true});
            skLineSegment(sketch, "E167.0", {"start": v(470.4, -86.56) * mm, "end": v(470.4, -147.09) * mm});
            skLineSegment(sketch, "E167.1", {"start": v(470.4, -147.09) * mm, "end": v(417.98, -177.35) * mm});
            skLineSegment(sketch, "E167.2", {"start": v(417.98, -177.35) * mm, "end": v(365.56, -147.09) * mm});
            skLineSegment(sketch, "E167.3", {"start": v(365.56, -147.09) * mm, "end": v(365.56, -86.56) * mm});
            skLineSegment(sketch, "E167.4", {"start": v(365.56, -86.56) * mm, "end": v(417.98, -56.3) * mm});
            skLineSegment(sketch, "E167.5", {"start": v(417.98, -56.3) * mm, "end": v(470.4, -86.56) * mm});
            skPoint(sketch, "E167.0.midPoint", {"position": v(470.4, -116.83) * mm});
            skCircle(sketch, "E168.cCircle", {"center": v(487.6, -267.75) * mm, "radius": 41.65 * mm, "construction": true});
            skLineSegment(sketch, "E168.0", {"start": v(529.26, -237.5) * mm, "end": v(529.26, -298.02) * mm});
            skLineSegment(sketch, "E168.1", {"start": v(529.26, -298.02) * mm, "end": v(471.7, -316.72) * mm});
            skLineSegment(sketch, "E168.2", {"start": v(471.7, -316.72) * mm, "end": v(436.12, -267.75) * mm});
            skLineSegment(sketch, "E168.3", {"start": v(436.12, -267.75) * mm, "end": v(471.7, -218.79) * mm});
            skLineSegment(sketch, "E168.4", {"start": v(471.7, -218.79) * mm, "end": v(529.26, -237.5) * mm});
            skPoint(sketch, "E168.0.midPoint", {"position": v(529.26, -267.75) * mm});
            skLineSegment(sketch, "E169", {"start": v(299.36, 23.3) * mm, "end": v(299.36, 83.83) * mm});
            skLineSegment(sketch, "E170", {"start": v(299.36, 83.83) * mm, "end": v(256.71, 53.57) * mm});
            skLineSegment(sketch, "E171", {"start": v(256.71, 53.57) * mm, "end": v(299.36, 23.3) * mm});
            skLineSegment(sketch, "E172", {"start": v(369.15, 78.21) * mm, "end": v(369.15, 17.69) * mm});
            skLineSegment(sketch, "E173", {"start": v(369.15, 17.69) * mm, "end": v(315.2, 47.95) * mm});
            skLineSegment(sketch, "E174", {"start": v(315.2, 47.95) * mm, "end": v(369.15, 78.21) * mm});
            skLineSegment(sketch, "E175", {"start": v(506.4, 7.23) * mm, "end": v(506.4, -145.1) * mm, "construction": true});
            skLineSegment(sketch, "E176", {"start": v(506.4, -41.44) * mm, "end": v(499.73, -42.1) * mm});
            skLineSegment(sketch, "E177", {"start": v(497.54, -40.3) * mm, "end": v(497.44, -39.31) * mm});
            skLineSegment(sketch, "E178", {"start": v(497.44, -39.31) * mm, "end": v(500.43, -39.02) * mm});
            skLineSegment(sketch, "E179", {"start": v(500.43, -39.02) * mm, "end": v(500.13, -36.03) * mm});
            skLineSegment(sketch, "E180", {"start": v(500.13, -36.03) * mm, "end": v(506.4, -35.41) * mm});
            skLineSegment(sketch, "E181", {"start": v(500.28, -39.03) * mm, "end": v(506.4, -38.43) * mm, "construction": true});
            skPoint(sketch, "E181.startSnap0", {"position": v(500.28, -37.52) * mm});
            skLineSegment(sketch, "E182", {"start": v(506.4, -53.5) * mm, "end": v(498.72, -54.47) * mm});
            skLineSegment(sketch, "E183", {"start": v(498.72, -54.47) * mm, "end": v(498.46, -52.48) * mm});
            skLineSegment(sketch, "E184", {"start": v(498.46, -52.48) * mm, "end": v(501.44, -52.1) * mm});
            skLineSegment(sketch, "E185", {"start": v(501.44, -52.1) * mm, "end": v(501.06, -49.13) * mm});
            skLineSegment(sketch, "E186", {"start": v(501.06, -49.13) * mm, "end": v(506.4, -48.45) * mm});
            skLineSegment(sketch, "E187", {"start": v(501.25, -52.13) * mm, "end": v(506.4, -51.48) * mm, "construction": true});
            skPoint(sketch, "E187.startSnap0", {"position": v(501.25, -50.62) * mm});
            skLineSegment(sketch, "E188", {"start": v(506.4, -71.26) * mm, "end": v(497.7, -72.3) * mm});
            skLineSegment(sketch, "E189", {"start": v(497.7, -72.3) * mm, "end": v(497.46, -70.32) * mm});
            skLineSegment(sketch, "E190", {"start": v(497.46, -70.32) * mm, "end": v(500.44, -69.96) * mm});
            skLineSegment(sketch, "E191", {"start": v(500.44, -69.96) * mm, "end": v(500.09, -66.98) * mm});
            skLineSegment(sketch, "E192", {"start": v(500.09, -66.98) * mm, "end": v(506.4, -66.23) * mm});
            skLineSegment(sketch, "E193", {"start": v(500.27, -69.98) * mm, "end": v(506.4, -69.25) * mm, "construction": true});
            skPoint(sketch, "E193.startSnap0", {"position": v(500.27, -68.47) * mm});
            skLineSegment(sketch, "E194", {"start": v(506.4, -89.42) * mm, "end": v(499.83, -90.25) * mm});
            skLineSegment(sketch, "E195", {"start": v(497.6, -88.51) * mm, "end": v(497.47, -87.52) * mm});
            skLineSegment(sketch, "E196", {"start": v(497.47, -87.52) * mm, "end": v(500.45, -87.15) * mm});
            skLineSegment(sketch, "E197", {"start": v(500.45, -87.15) * mm, "end": v(500.07, -84.17) * mm});
            skLineSegment(sketch, "E198", {"start": v(500.07, -84.17) * mm, "end": v(506.4, -83.37) * mm});
            skLineSegment(sketch, "E199", {"start": v(500.26, -87.17) * mm, "end": v(506.4, -86.4) * mm, "construction": true});
            skPoint(sketch, "E199.startSnap0", {"position": v(500.26, -85.66) * mm});
            skLineSegment(sketch, "E200.MirrorCS", {"start": v(512.36, -69.96) * mm, "end": v(512.71, -66.98) * mm});
            skLineSegment(sketch, "E201.MirrorCS", {"start": v(515.34, -70.32) * mm, "end": v(512.36, -69.96) * mm});
            skLineSegment(sketch, "E202.MirrorCS", {"start": v(512.35, -87.15) * mm, "end": v(512.73, -84.17) * mm});
            skLineSegment(sketch, "E203.MirrorCS", {"start": v(515.33, -87.52) * mm, "end": v(512.35, -87.15) * mm});
            skLineSegment(sketch, "E204.MirrorCS", {"start": v(515.2, -88.51) * mm, "end": v(515.33, -87.52) * mm});
            skLineSegment(sketch, "E205.MirrorCS", {"start": v(511.38, -38.92) * mm, "end": v(511.67, -35.93) * mm});
            skLineSegment(sketch, "E206.MirrorCS", {"start": v(515.36, -39.31) * mm, "end": v(511.38, -38.92) * mm});
            skLineSegment(sketch, "E207.MirrorCS", {"start": v(515.26, -40.3) * mm, "end": v(515.36, -39.31) * mm});
            skLineSegment(sketch, "E208.MirrorCS", {"start": v(511.36, -52.1) * mm, "end": v(511.74, -49.13) * mm});
            skLineSegment(sketch, "E209.MirrorCS", {"start": v(514.34, -52.48) * mm, "end": v(511.36, -52.1) * mm});
            skLineSegment(sketch, "E210.MirrorCS", {"start": v(515.1, -72.3) * mm, "end": v(515.34, -70.32) * mm});
            skLineSegment(sketch, "E211.MirrorCS", {"start": v(514.09, -54.47) * mm, "end": v(514.34, -52.48) * mm});
            skLineSegment(sketch, "E212.MirrorCS", {"start": v(512.54, -69.98) * mm, "end": v(506.4, -69.25) * mm, "construction": true});
            skLineSegment(sketch, "E213.MirrorCS", {"start": v(511.67, -35.93) * mm, "end": v(506.4, -35.41) * mm});
            skLineSegment(sketch, "E214.MirrorCS", {"start": v(512.52, -39.03) * mm, "end": v(506.4, -38.43) * mm, "construction": true});
            skLineSegment(sketch, "E215.MirrorCS", {"start": v(506.4, -41.44) * mm, "end": v(513.07, -42.1) * mm});
            skLineSegment(sketch, "E216.MirrorCS", {"start": v(511.74, -49.13) * mm, "end": v(506.4, -48.45) * mm});
            skLineSegment(sketch, "E217.MirrorCS", {"start": v(511.55, -52.13) * mm, "end": v(506.4, -51.48) * mm, "construction": true});
            skLineSegment(sketch, "E218.MirrorCS", {"start": v(506.4, -53.5) * mm, "end": v(514.09, -54.47) * mm});
            skLineSegment(sketch, "E219.MirrorCS", {"start": v(512.71, -66.98) * mm, "end": v(506.4, -66.23) * mm});
            skLineSegment(sketch, "E220.MirrorCS", {"start": v(506.4, -71.26) * mm, "end": v(515.1, -72.3) * mm});
            skLineSegment(sketch, "E221.MirrorCS", {"start": v(512.73, -84.17) * mm, "end": v(506.4, -83.37) * mm});
            skLineSegment(sketch, "E222.MirrorCS", {"start": v(512.54, -87.17) * mm, "end": v(506.4, -86.4) * mm, "construction": true});
            skLineSegment(sketch, "E223.MirrorCS", {"start": v(506.4, -89.42) * mm, "end": v(512.97, -90.25) * mm});
            skPoint(sketch, "E224.MirrorP", {"position": v(512.52, -37.52) * mm});
            skPoint(sketch, "E225.MirrorP", {"position": v(511.55, -50.62) * mm});
            skPoint(sketch, "E226.MirrorP", {"position": v(512.54, -68.47) * mm});
            skPoint(sketch, "E227.MirrorP", {"position": v(512.54, -85.66) * mm});
            skArc(sketch, "E228", {"start": v(498.72, -54.47) * mm, "mid": v(506.4, -55.5) * mm, "end": v(514.09, -54.47) * mm});
            skPoint(sketch, "E228.third.point", {"position": v(506.4, -55.5) * mm});
            skArc(sketch, "E229", {"start": v(497.7, -72.3) * mm, "mid": v(506.4, -73.26) * mm, "end": v(515.1, -72.3) * mm});
            skPoint(sketch, "E229.third.point", {"position": v(505.22, -73.25) * mm});
            skPoint(sketch, "E230.visualSharp", {"position": v(497.74, -42.3) * mm});
            skArc(sketch, "E230.filletArc", {"start": v(497.54, -40.3) * mm, "mid": v(498.27, -41.66) * mm, "end": v(499.73, -42.1) * mm});
            skPoint(sketch, "E231.visualSharp", {"position": v(515.06, -42.3) * mm});
            skArc(sketch, "E231.filletArc", {"start": v(513.07, -42.1) * mm, "mid": v(514.54, -41.66) * mm, "end": v(515.26, -40.3) * mm});
            skPoint(sketch, "E232.visualSharp", {"position": v(497.85, -90.5) * mm});
            skArc(sketch, "E232.filletArc", {"start": v(497.6, -88.51) * mm, "mid": v(498.36, -89.84) * mm, "end": v(499.83, -90.25) * mm});
            skPoint(sketch, "E233.visualSharp", {"position": v(514.95, -90.5) * mm});
            skArc(sketch, "E233.filletArc", {"start": v(512.97, -90.25) * mm, "mid": v(514.45, -89.84) * mm, "end": v(515.2, -88.51) * mm});
            skSolve(sketch);
        }
        {
            var Q0;
            Q0 = qSketchRegion(id + "F3", true);
            extrude(context, id + "F4", {"entities" : qUnion([Q0]), "depth" : 3 * mm});
        }
        {
            var Q0;
            Q0=makeQuery(id+"F4.opExtrude","CAP_FACE",FACE,{"disambiguationData":[OSD([sQuery(id+"F3.wireOp",EDGE,"E172"),sQuery(id+"F3.wireOp",EDGE,"E173"),sQuery(id+"F3.wireOp",EDGE,"E174")])],"isStart":false});
            var sketch = newSketch(context, id + "F5", { "sketchPlane" : qUnion([Q0])});
            skLineSegment(sketch, "E234.0", {"start": v(299.36, 83.83) * mm, "end": v(256.71, 53.57) * mm, "construction": true});
            skLineSegment(sketch, "E234.1", {"start": v(256.71, 53.57) * mm, "end": v(299.36, 23.3) * mm, "construction": true});
            skLineSegment(sketch, "E234.2", {"start": v(369.15, 17.69) * mm, "end": v(315.2, 47.95) * mm, "construction": true});
            skLineSegment(sketch, "E234.3", {"start": v(315.2, 47.95) * mm, "end": v(369.15, 78.21) * mm, "construction": true});
            skLineSegment(sketch, "E234.5", {"start": v(299.36, 23.3) * mm, "end": v(299.36, 83.83) * mm, "construction": true});
            skLineSegment(sketch, "E234.6", {"start": v(299.36, 83.83) * mm, "end": v(256.71, 53.57) * mm, "construction": true});
            skLineSegment(sketch, "E234.7", {"start": v(256.71, 53.57) * mm, "end": v(299.36, 23.3) * mm, "construction": true});
            skLineSegment(sketch, "E234.9", {"start": v(369.15, 78.21) * mm, "end": v(369.15, 17.69) * mm, "construction": true});
            skLineSegment(sketch, "E234.10", {"start": v(369.15, 17.69) * mm, "end": v(315.2, 47.95) * mm, "construction": true});
            skLineSegment(sketch, "E234.11", {"start": v(315.2, 47.95) * mm, "end": v(369.15, 78.21) * mm, "construction": true});
            skLineSegment(sketch, "E234.14", {"start": v(299.36, 23.3) * mm, "end": v(299.36, 83.83) * mm, "construction": true});
            skLineSegment(sketch, "E234.17", {"start": v(369.15, 78.21) * mm, "end": v(369.15, 17.69) * mm, "construction": true});
            skPoint(sketch, "E235", {"position": v(278.04, 68.7) * mm});
            skPoint(sketch, "E236", {"position": v(278.04, 38.44) * mm});
            skPoint(sketch, "E237", {"position": v(299.36, 53.57) * mm});
            skLineSegment(sketch, "E238.bottom", {"start": v(299.36, 55.07) * mm, "end": v(294.36, 55.07) * mm});
            skLineSegment(sketch, "E238.top", {"start": v(299.36, 52.07) * mm, "end": v(294.36, 52.07) * mm});
            skLineSegment(sketch, "E238.left", {"start": v(299.36, 55.07) * mm, "end": v(299.36, 52.07) * mm});
            skLineSegment(sketch, "E238.right", {"start": v(294.36, 55.07) * mm, "end": v(294.36, 52.07) * mm});
            skLineSegment(sketch, "E239", {"start": v(279.26, 69.57) * mm, "end": v(282.15, 65.5) * mm});
            skLineSegment(sketch, "E240", {"start": v(282.15, 65.5) * mm, "end": v(279.7, 63.76) * mm});
            skLineSegment(sketch, "E241", {"start": v(279.7, 63.76) * mm, "end": v(276.81, 67.83) * mm});
            skLineSegment(sketch, "E242", {"start": v(276.81, 67.83) * mm, "end": v(279.26, 69.57) * mm});
            skLineSegment(sketch, "E243", {"start": v(276.81, 39.3) * mm, "end": v(279.7, 43.39) * mm});
            skLineSegment(sketch, "E244", {"start": v(279.7, 43.39) * mm, "end": v(282.15, 41.65) * mm});
            skLineSegment(sketch, "E245", {"start": v(282.15, 41.65) * mm, "end": v(279.26, 37.57) * mm});
            skLineSegment(sketch, "E246", {"start": v(279.26, 37.57) * mm, "end": v(276.81, 39.3) * mm});
            skPoint(sketch, "E247", {"position": v(342.18, 63.08) * mm});
            skPoint(sketch, "E248", {"position": v(369.15, 47.95) * mm});
            skPoint(sketch, "E249", {"position": v(342.18, 32.82) * mm});
            skLineSegment(sketch, "E250", {"start": v(369.15, 49.45) * mm, "end": v(363.15, 49.45) * mm});
            skLineSegment(sketch, "E251", {"start": v(363.15, 49.45) * mm, "end": v(363.15, 46.45) * mm});
            skLineSegment(sketch, "E252", {"start": v(363.15, 46.45) * mm, "end": v(369.15, 46.45) * mm});
            skLineSegment(sketch, "E253", {"start": v(369.15, 46.45) * mm, "end": v(369.15, 49.45) * mm});
            skLineSegment(sketch, "E254", {"start": v(343.48, 63.81) * mm, "end": v(346.42, 58.58) * mm});
            skLineSegment(sketch, "E255", {"start": v(346.42, 58.58) * mm, "end": v(343.8, 57.11) * mm});
            skLineSegment(sketch, "E256", {"start": v(343.8, 57.11) * mm, "end": v(340.87, 62.35) * mm});
            skLineSegment(sketch, "E257", {"start": v(340.87, 62.35) * mm, "end": v(343.48, 63.81) * mm});
            skLineSegment(sketch, "E258", {"start": v(340.87, 33.55) * mm, "end": v(343.8, 38.78) * mm});
            skLineSegment(sketch, "E259", {"start": v(343.8, 38.78) * mm, "end": v(346.42, 37.32) * mm});
            skLineSegment(sketch, "E260", {"start": v(346.42, 37.32) * mm, "end": v(343.48, 32.08) * mm});
            skLineSegment(sketch, "E261", {"start": v(343.48, 32.08) * mm, "end": v(340.87, 33.55) * mm});
            skSolve(sketch);
        }
        {
            var Q0;
            Q0 = qSketchRegion(id + "F5", true);
            extrude(context, id + "F6", {"entities" : qUnion([Q0]), "operationType" : NewBodyOperationType.REMOVE, "oppositeDirection" : true, "depth" : 25 * mm});
        }
    });
